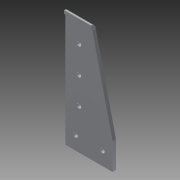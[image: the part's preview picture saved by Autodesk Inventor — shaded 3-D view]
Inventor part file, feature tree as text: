
AUTODESK INVENTOR PART (.ipt)
format: ipt  version: 2014 (Build 180170000, 170)  size: 220,672 bytes
history: native  units: in
note: dims shown in document units (in); Inventor stores cm internally (conversion verified against a paired STEP export)
features: other x6, sheet_metal_op x4, sketch x3, fillet x2, plane x1
ambient origin geometry x8: Origin, YZ Plane, XZ Plane, XY Plane, X Axis, Y Axis, Z Axis, Center Point
bodies: Solid1 (feature_tree)
feature tree (16):
  sheet_metal_op  "Face1"
  plane  "Work Plane1"
  sheet_metal_op  "Flange2"
  fillet  "Fillet4"  Radius=0.163in
  fillet  "Fillet5"  Radius=0.125in
  sketch  "Sketch1"  dims[d4=0.7874in d6=1.0in d7=0.3937in d9=1.0in d11=0.125in]
  other  "Plate1"
  sketch  "Sketch5"  dims[d22=0.5in]
  other  "Plate3"
  sheet_metal_op  "Bend2"
  sheet_metal_op  "Corner2"
  sketch  "Sketch6"  dims[d28=0.187in d29=0.25in d34=0.75in d38=0.5in d39=1.5in d40=1.1811in d42=1.0in d43=0.3937in d45=1.0in d47=0.125in d48=0.25in d49=0.25in d50=0.375in d51=0.125in d52=0.0in d54=1.0in d55=4.1875in d56=1.0in d57=1.75in d58=0.375in d59=0.125in d60=0.0625in d61=0.25in d62=0.125in d63=1.0in d64=90.0deg d65=0.05in d66=0.5in d67=0.125in d68=0.125in d69=0.187in d70=0.25in d71=0.75in d72=0.125in d73=0.25in d74=0.25in d75=0.375in d76=0.5in d77=0.125in d78=0.0in d79=0.125in d80=0.5in d0=0.125in d1=0.125in d3=0.0in]
  other  "Cut3"
  other  "Cut4"
  other  "Definition1"
  other  "Cut1"
